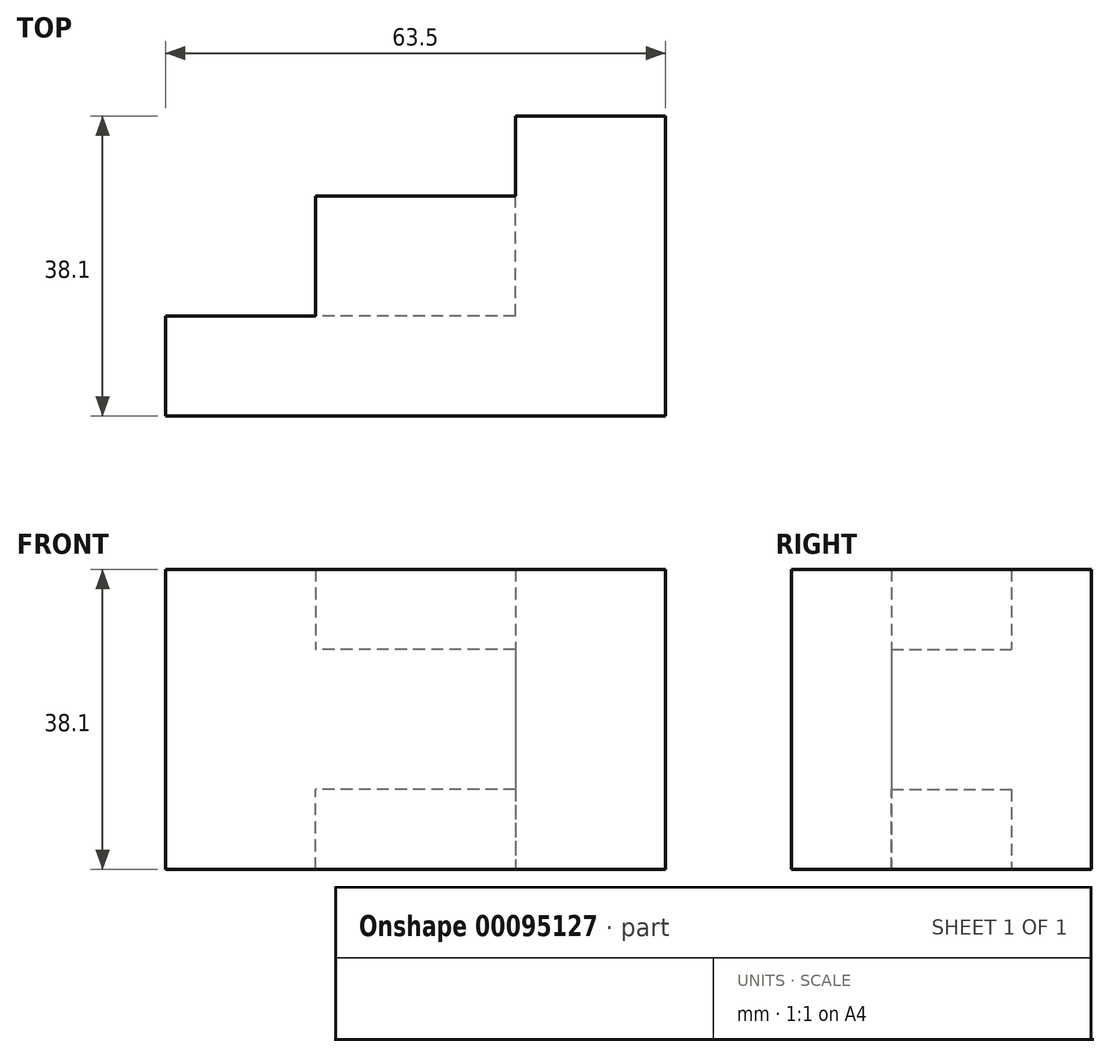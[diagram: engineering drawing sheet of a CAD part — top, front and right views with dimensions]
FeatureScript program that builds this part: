
annotation { "Feature Type Name" : "Feature", "Feature Type Description" : "" }
export const myFeature = defineFeature(function(context is Context, id is Id, definition is map)
    precondition{}
    {
        {
            var Q0;
            Q0=qCreatedBy(makeId("Front.planeOp"),FACE);
            var sketch = newSketch(context, id + "F0", { "sketchPlane" : qUnion([Q0])});
            skLineSegment(sketch, "E0.bottom", {"start": v(31.75, 19.05) * mm, "end": v(-31.75, 19.05) * mm});
            skLineSegment(sketch, "E0.top", {"start": v(31.75, -19.05) * mm, "end": v(-31.75, -19.05) * mm});
            skLineSegment(sketch, "E0.left", {"start": v(31.75, 19.05) * mm, "end": v(31.75, -19.05) * mm});
            skLineSegment(sketch, "E0.right", {"start": v(-31.75, 19.05) * mm, "end": v(-31.75, -19.05) * mm});
            skPoint(sketch, "E0.middle", {"position": v(0, 0) * mm});
            skSolve(sketch);
        }
        {
            var Q0;
            Q0=makeQuery(id+"F0.imprint","IMPRINT",FACE,{"disambiguationData":[TD([[makeQuery(id+"F0.imprint","IMPRINT",EDGE,{"derivedFrom":sQuery(id+"F0.wireOp",EDGE,"E0.bottom")}),1.0]])]});
            extrude(context, id + "F1", {"entities" : qUnion([Q0]), "depth" : 38.1 * mm});
        }
        {
            var Q0;
            Q0=makeQuery(id+"F1.opExtrude","CAP_FACE",FACE,{"disambiguationData":[OSD([sQuery(id+"F0.wireOp",EDGE,"E0.bottom"),sQuery(id+"F0.wireOp",EDGE,"E0.top"),sQuery(id+"F0.wireOp",EDGE,"E0.left"),sQuery(id+"F0.wireOp",EDGE,"E0.right")])],"isStart":true});
            var sketch = newSketch(context, id + "F2", { "sketchPlane" : qUnion([Q0])});
            skLineSegment(sketch, "E1.bottom", {"start": v(-31.75, 19.05) * mm, "end": v(-12.7, 19.05) * mm});
            skLineSegment(sketch, "E1.top", {"start": v(-31.75, -19.05) * mm, "end": v(-12.7, -19.05) * mm});
            skLineSegment(sketch, "E1.left", {"start": v(-31.75, 19.05) * mm, "end": v(-31.75, -19.05) * mm});
            skLineSegment(sketch, "E1.right", {"start": v(-12.7, 19.05) * mm, "end": v(-12.7, -19.05) * mm});
            skLineSegment(sketch, "E2.bottom", {"start": v(-12.7, 19.05) * mm, "end": v(12.7, 19.05) * mm});
            skLineSegment(sketch, "E2.top", {"start": v(-12.7, 8.89) * mm, "end": v(12.7, 8.89) * mm});
            skLineSegment(sketch, "E2.left", {"start": v(-12.7, 19.05) * mm, "end": v(-12.7, 8.89) * mm});
            skLineSegment(sketch, "E2.right", {"start": v(12.7, 19.05) * mm, "end": v(12.7, 8.89) * mm});
            skLineSegment(sketch, "E3.bottom", {"start": v(-12.7, -19.05) * mm, "end": v(12.7, -19.05) * mm});
            skLineSegment(sketch, "E3.top", {"start": v(-12.7, -8.9) * mm, "end": v(12.7, -8.9) * mm});
            skLineSegment(sketch, "E3.left", {"start": v(-12.7, -19.05) * mm, "end": v(-12.7, -8.9) * mm});
            skLineSegment(sketch, "E3.right", {"start": v(12.7, -19.05) * mm, "end": v(12.7, -8.9) * mm});
            skSolve(sketch);
        }
        {
            var Q0;
            Q0=makeQuery(id+"F2.imprint","IMPRINT",FACE,{"disambiguationData":[TD([[makeQuery(id+"F2.imprint","IMPRINT",EDGE,{"derivedFrom":sQuery(id+"F2.wireOp",EDGE,"E2.bottom")}),-1.0]])]});
            var Q1;
            Q1=makeQuery(id+"F2.imprint","IMPRINT",FACE,{"disambiguationData":[TD([[makeQuery(id+"F2.imprint","IMPRINT",EDGE,{"derivedFrom":sQuery(id+"F2.wireOp",EDGE,"E3.bottom")}),1.0]])]});
            extrude(context, id + "F3", {"entities" : qUnion([Q0, Q1]), "operationType" : NewBodyOperationType.REMOVE, "oppositeDirection" : true, "depth" : 10.16 * mm});
        }
        {
            var Q0;
            Q0=makeQuery(id+"F1.opExtrude","CAP_FACE",FACE,{"disambiguationData":[OSD([sQuery(id+"F0.wireOp",EDGE,"E0.bottom"),sQuery(id+"F0.wireOp",EDGE,"E0.top"),sQuery(id+"F0.wireOp",EDGE,"E0.left"),sQuery(id+"F0.wireOp",EDGE,"E0.right")])],"isStart":true});
            var sketch = newSketch(context, id + "F4", { "sketchPlane" : qUnion([Q0])});
            skLineSegment(sketch, "E4.bottom", {"start": v(31.75, 19.05) * mm, "end": v(-12.7, 19.05) * mm});
            skLineSegment(sketch, "E4.top", {"start": v(31.75, -19.05) * mm, "end": v(-12.7, -19.05) * mm});
            skLineSegment(sketch, "E4.left", {"start": v(31.75, 19.05) * mm, "end": v(31.75, -19.05) * mm});
            skLineSegment(sketch, "E4.right", {"start": v(-12.7, 19.05) * mm, "end": v(-12.7, -19.05) * mm});
            skSolve(sketch);
        }
        {
            var Q0;
            {var subQ0=sQuery(id+"F4.wireOp",EDGE,"E4.left");Q0=makeQuery(id+"F4.imprint","IMPRINT",FACE,{"disambiguationData":[TD([[makeQuery(id+"F4.imprint","IMPRINT",EDGE,{"derivedFrom":subQ0}),-1.0]])]});}
            extrude(context, id + "F5", {"entities" : qUnion([Q0]), "operationType" : NewBodyOperationType.REMOVE, "oppositeDirection" : true, "depth" : 25.4 * mm});
        }
    });
